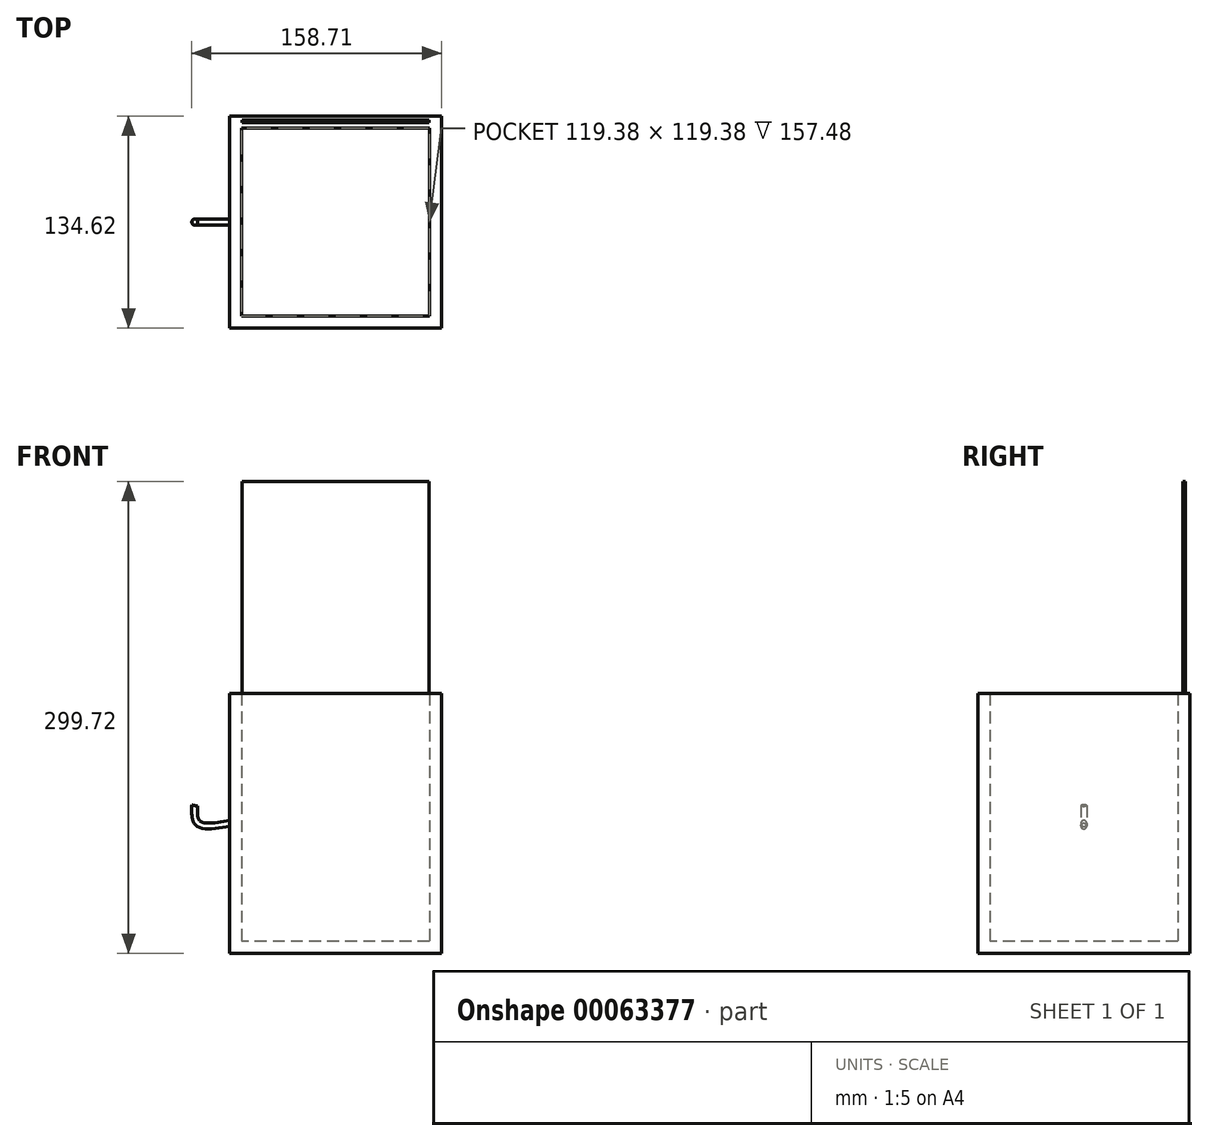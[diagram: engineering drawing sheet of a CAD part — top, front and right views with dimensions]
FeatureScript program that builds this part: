
annotation { "Feature Type Name" : "Feature", "Feature Type Description" : "" }
export const myFeature = defineFeature(function(context is Context, id is Id, definition is map)
    precondition{}
    {
        {
            var Q0;
            Q0=qCreatedBy(makeId("Top.planeOp"),FACE);
            var sketch = newSketch(context, id + "F0", { "sketchPlane" : qUnion([Q0])});
            skLineSegment(sketch, "E0.rect.bottom", {"start": v(67.3, 67.31) * mm, "end": v(-67.3, 67.31) * mm});
            skLineSegment(sketch, "E0.rect.top", {"start": v(67.3, -67.31) * mm, "end": v(-67.3, -67.31) * mm});
            skLineSegment(sketch, "E0.rect.left", {"start": v(67.3, 67.3) * mm, "end": v(67.31, -67.3) * mm});
            skLineSegment(sketch, "E0.rect.right", {"start": v(-67.31, 67.3) * mm, "end": v(-67.3, -67.3) * mm});
            skPoint(sketch, "E0.rect.middle", {"position": v(0, 0) * mm});
            skSolve(sketch);
        }
        {
            var Q0;
            Q0 = qSketchRegion(id + "F0", true);
            extrude(context, id + "F1", {"entities" : qUnion([Q0]), "endBound" : BoundingType.SYMMETRIC, "depth" : 165.1 * mm});
        }
        {
            var Q0;
            Q0=makeQuery(id+"F1.opExtrude","CAP_FACE",FACE,{"disambiguationData":[OSD([sQuery(id+"F0.wireOp",EDGE,"E0.rect.bottom"),sQuery(id+"F0.wireOp",EDGE,"E0.rect.top"),sQuery(id+"F0.wireOp",EDGE,"E0.rect.left"),sQuery(id+"F0.wireOp",EDGE,"E0.rect.right")])],"isStart":false});
            shell(context, id + "F2", {"entities" : qUnion([Q0]), "thickness" : 7.62 * mm});
        }
        {
            var Q0;
            Q0=makeQuery(id+"F1.opExtrude","CAP_FACE",FACE,{"disambiguationData":[OSD([sQuery(id+"F0.wireOp",EDGE,"E0.rect.bottom"),sQuery(id+"F0.wireOp",EDGE,"E0.rect.top"),sQuery(id+"F0.wireOp",EDGE,"E0.rect.left"),sQuery(id+"F0.wireOp",EDGE,"E0.rect.right")])],"isStart":false});
            var sketch = newSketch(context, id + "F3", { "sketchPlane" : qUnion([Q0])});
            skLineSegment(sketch, "E1.rect.bottom", {"start": v(-59.28, 64.63) * mm, "end": v(59.28, 64.63) * mm});
            skLineSegment(sketch, "E1.rect.top", {"start": v(-59.28, 63.06) * mm, "end": v(59.28, 63.06) * mm});
            skLineSegment(sketch, "E1.rect.left", {"start": v(-59.28, 64.63) * mm, "end": v(-59.28, 63.06) * mm});
            skLineSegment(sketch, "E1.rect.right", {"start": v(59.28, 64.63) * mm, "end": v(59.28, 63.06) * mm});
            skPoint(sketch, "E1.rect.middle", {"position": v(0, 63.84) * mm});
            skSolve(sketch);
        }
        {
            var Q0;
            Q0 = qSketchRegion(id + "F3", true);
            extrude(context, id + "F4", {"entities" : qUnion([Q0]), "operationType" : NewBodyOperationType.ADD, "depth" : 134.62 * mm});
        }
        {
            var Q0;
            Q0=qCreatedBy(makeId("Front.planeOp"),FACE);
            var sketch = newSketch(context, id + "F5", { "sketchPlane" : qUnion([Q0])});
            skPoint(sketch, "E2.1.internal.snap0", {"position": v(-67.31, 0) * mm});
            skFitSpline(sketch, "E2", {"points": [v(-67.3, 0) * mm, v(-87.23, 0) * mm, v(-89.45, 11.35) * mm], "startDerivative": vector(-43.6, -7.45) * mm, "endDerivative": vector(1.34, 31.92) * mm});
            skPoint(sketch, "E3.orphan", {"position": v(-67.31, 82.55) * mm});
            skPoint(sketch, "E4.0.end.orphan", {"position": v(-67.31, -82.55) * mm});
            skSolve(sketch);
        }
        {
            var Q0;
            Q0=makeQuery(id+"F1.opExtrude","SWEPT_FACE",FACE,{"disambiguationData":[OSD([sQuery(id+"F0.wireOp",EDGE,"E0.rect.right")])]});
            var sketch = newSketch(context, id + "F6", { "sketchPlane" : qUnion([Q0])});
            skCircle(sketch, "E5", {"center": v(0, 0) * mm, "radius": 1.87 * mm});
            skSolve(sketch);
        }
        {
            var Q0;
            Q0=makeQuery(id+"F6.imprint","IMPRINT",FACE,{"disambiguationData":[TD([[makeQuery(id+"F6.imprint","IMPRINT",EDGE,{"derivedFrom":sQuery(id+"F6.wireOp",EDGE,"E5")}),1.0]])]});
            var Q1;
            Q1=sQuery(id+"F5.wireOp",EDGE,"E2");
            sweep(context, id + "F7", {"operationType" : NewBodyOperationType.ADD, "profiles" : qUnion([Q0]), "path" : qUnion([Q1])});
        }
    });
